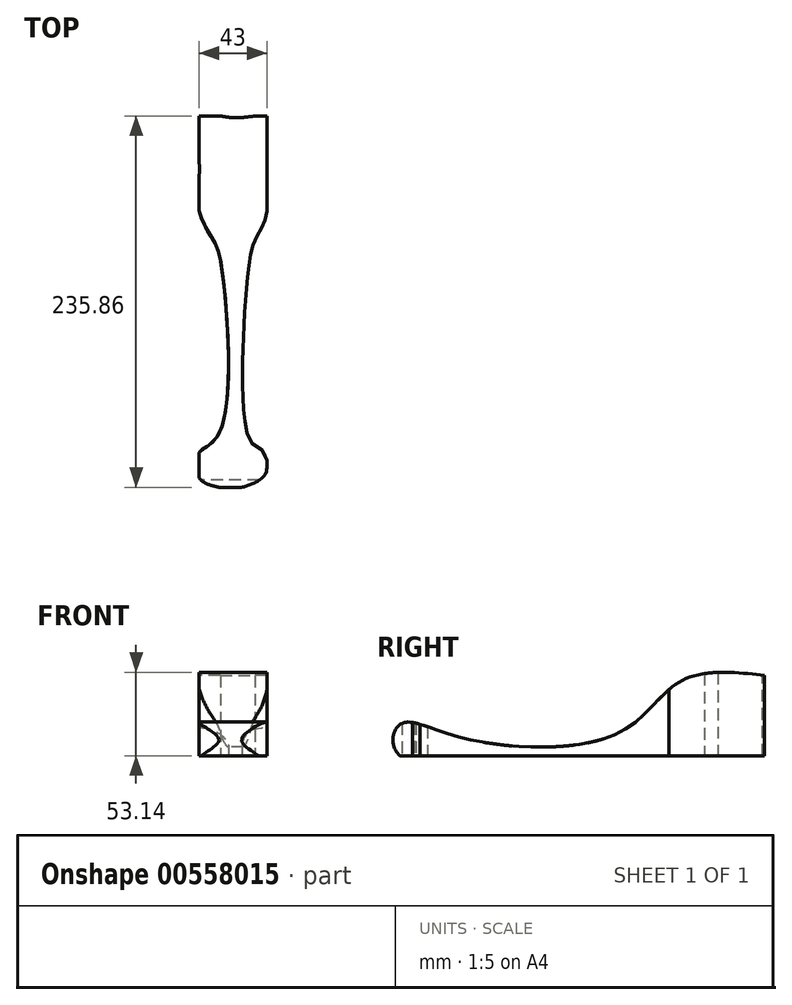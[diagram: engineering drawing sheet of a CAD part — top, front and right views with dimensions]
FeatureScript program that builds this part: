
annotation { "Feature Type Name" : "Feature", "Feature Type Description" : "" }
export const myFeature = defineFeature(function(context is Context, id is Id, definition is map)
    precondition{}
    {
        {
            var Q0;
            Q0=qCreatedBy(makeId("Right.planeOp"),FACE);
            var sketch = newSketch(context, id + "F0", { "sketchPlane" : qUnion([Q0])});
            skLineSegment(sketch, "E0", {"start": v(92.45, 31.06) * mm, "end": v(92.45, -19.95) * mm});
            skLineSegment(sketch, "E1", {"start": v(92.45, -19.95) * mm, "end": v(-138.9, -19.95) * mm});
            skFitSpline(sketch, "E2", {"points": [v(-138.9, -19.95) * mm, v(-138.9, 0) * mm, v(-103.55, -7.32) * mm, v(0, -5.3) * mm, v(41.42, 28.54) * mm, v(92.45, 31.06) * mm], "startDerivative": vector(-166.98, 154.86) * mm, "endDerivative": vector(217.92, -29.02) * mm});
            skSolve(sketch);
        }
        {
            var Q0;
            Q0=makeQuery(id+"F0.imprint","IMPRINT",FACE,{"disambiguationData":[TD([[makeQuery(id+"F0.imprint","IMPRINT",EDGE,{"derivedFrom":sQuery(id+"F0.wireOp",EDGE,"E0")}),-1.0]])]});
            extrude(context, id + "F1", {"entities" : qUnion([Q0]), "depth" : 43 * mm, "offsetDistance" : 25 * mm});
        }
        {
            var Q0;
            Q0=makeQuery(id+"F1.opExtrude","SWEPT_BODY",BODY,{"disambiguationData":[OSD([sQuery(id+"F0.wireOp",EDGE,"E0"),sQuery(id+"F0.wireOp",EDGE,"E1"),sQuery(id+"F0.wireOp",EDGE,"E2")])]});
            transform(context, id + "F2", {"entities" : qUnion([Q0]), "transformType" : TransformType.TRANSLATION_3D, "dx" : 0 * mm, "dy" : 0 * mm, "dz" : 21 * mm, "makeCopy" : false});
        }
        {
            var Q0;
            Q0=qCreatedBy(makeId("Top.planeOp"),FACE);
            var sketch = newSketch(context, id + "F3", { "sketchPlane" : qUnion([Q0])});
            skFitSpline(sketch, "E3", {"points": [v(43.44, 92.5) * mm, v(21.96, 91.35) * mm, v(0, 92.46) * mm, v(0, 62.94) * mm, v(0, 32.4) * mm, v(8.39, 14.54) * mm, v(13.6, 0) * mm, v(12.46, -109.67) * mm, v(0, -121.37) * mm, v(0, -129.26) * mm, v(0, -137.54) * mm, v(22.74, -143.98) * mm, v(41.04, -136.29) * mm, v(43.06, -129.95) * mm, v(41.12, -120.58) * mm, v(32.4, -114.05) * mm, v(31.94, 0) * mm, v(36.36, 15.5) * mm, v(42.94, 31.58) * mm, v(43.44, 81.4) * mm, v(43.44, 92.5) * mm]});
            skSolve(sketch);
        }
        {
            var Q0;
            Q0 = qSketchRegion(id + "F3", true);
            extrude(context, id + "F4", {"entities" : qUnion([Q0]), "operationType" : NewBodyOperationType.INTERSECT, "depth" : 55 * mm, "offsetDistance" : 25 * mm});
        }
        {
            var Q0;
            Q0=makeQuery(id+"F1.opExtrude","SWEPT_BODY",BODY,{"disambiguationData":[OSD([sQuery(id+"F0.wireOp",EDGE,"E0"),sQuery(id+"F0.wireOp",EDGE,"E1"),sQuery(id+"F0.wireOp",EDGE,"E2")])]});
            transform(context, id + "F5", {"entities" : qUnion([Q0]), "transformType" : TransformType.TRANSLATION_3D, "dx" : 0 * mm, "dy" : 0 * mm, "dz" : 0 * mm, "makeCopy" : true});
        }
        {
            var Q0;
            Q0=makeQuery(id+"F5.opPattern","COPY",BODY,{"derivedFrom":makeQuery(id+"F1.opExtrude","SWEPT_BODY",BODY,{"disambiguationData":[OSD([sQuery(id+"F0.wireOp",EDGE,"E0"),sQuery(id+"F0.wireOp",EDGE,"E1"),sQuery(id+"F0.wireOp",EDGE,"E2")])]}),"instanceName":"1"});
            deleteBodies(context, id + "F6", {"entities" : qUnion([Q0])});
        }
    });
